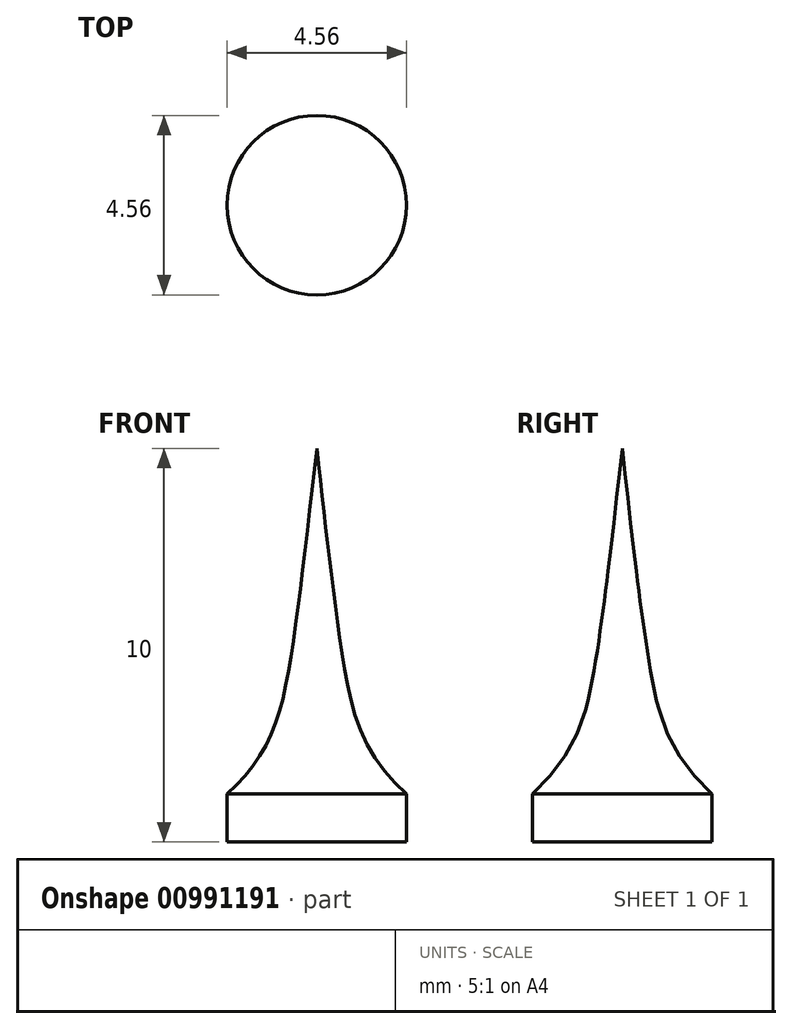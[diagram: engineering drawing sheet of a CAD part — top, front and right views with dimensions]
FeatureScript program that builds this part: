
annotation { "Feature Type Name" : "Feature", "Feature Type Description" : "" }
export const myFeature = defineFeature(function(context is Context, id is Id, definition is map)
    precondition{}
    {
        {
            var Q0;
            Q0=qCreatedBy(makeId("Front.planeOp"),FACE);
            var sketch = newSketch(context, id + "F0", { "sketchPlane" : qUnion([Q0])});
            skLineSegment(sketch, "E0", {"start": v(0, 0) * mm, "end": v(0, 10) * mm});
            skLineSegment(sketch, "E1", {"start": v(0, 0) * mm, "end": v(-5, 0) * mm});
            skFitSpline(sketch, "E2", {"points": [v(0, 10) * mm, v(-0.64, 4.82) * mm, v(-1.3, 2.44) * mm, v(-2.8, 0.85) * mm, v(-5, 0) * mm], "startDerivative": vector(-1.9, -17) * mm, "endDerivative": vector(-10.4, -2.96) * mm});
            skSolve(sketch);
        }
        {
            var Q0;
            Q0 = qSketchRegion(id + "F0", true);
            var Q1;
            Q1=sQuery(id+"F0.wireOp",EDGE,"E0");
            revolve(context, id + "F1", {"surfaceOperationType" : NewSurfaceOperationType.NEW, "entities" : qUnion([Q0]), "axis" : qUnion([Q1]), "revolveType" : RevolveType.FULL});
        }
        {
            var Q0;
            Q0=makeQuery(id+"F1.opRevolve","SWEPT_FACE",FACE,{"disambiguationData":[OSD([sQuery(id+"F0.wireOp",EDGE,"E1")])]});
            var sketch = newSketch(context, id + "F2", { "sketchPlane" : qUnion([Q0])});
            skCircle(sketch, "E3", {"center": v(0, 0) * mm, "radius": 2.28 * mm});
            skSolve(sketch);
        }
        {
            var Q0;
            Q0=makeQuery(id+"F2.imprint","IMPRINT",FACE,{"disambiguationData":[TD([[makeQuery(id+"F2.imprint","IMPRINT",EDGE,{"derivedFrom":sQuery(id+"F2.wireOp",EDGE,"E3")}),1.0]])]});
            extrude(context, id + "F3", {"entities" : qUnion([Q0]), "operationType" : NewBodyOperationType.INTERSECT, "oppositeDirection" : true, "depth" : 25 * mm, "offsetDistance" : 25 * mm});
        }
    });
